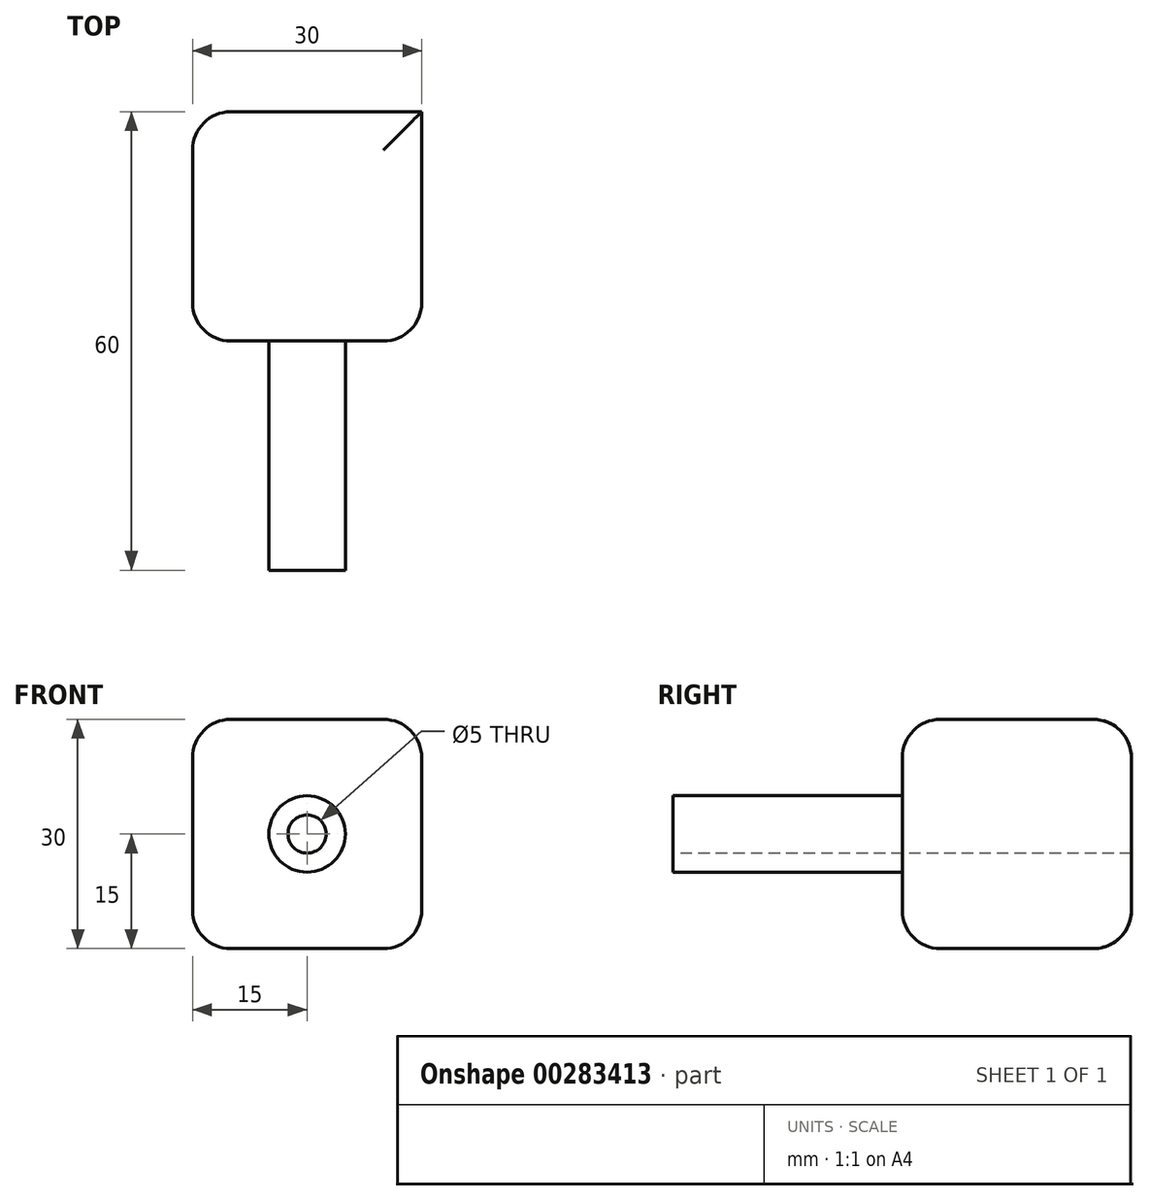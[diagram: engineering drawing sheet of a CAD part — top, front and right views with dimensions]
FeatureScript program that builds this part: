
annotation { "Feature Type Name" : "Feature", "Feature Type Description" : "" }
export const myFeature = defineFeature(function(context is Context, id is Id, definition is map)
    precondition{}
    {
        {
            var Q0;
            Q0=qCreatedBy(makeId("Front.planeOp"),FACE);
            var sketch = newSketch(context, id + "F0", { "sketchPlane" : qUnion([Q0])});
            skLineSegment(sketch, "E0.bottom", {"start": v(15, -15) * mm, "end": v(-15, -15) * mm});
            skLineSegment(sketch, "E0.top", {"start": v(15, 15) * mm, "end": v(-15, 15) * mm});
            skLineSegment(sketch, "E0.left", {"start": v(15, -15) * mm, "end": v(15, 15) * mm});
            skLineSegment(sketch, "E0.right", {"start": v(-15, -15) * mm, "end": v(-15, 15) * mm});
            skPoint(sketch, "E0.middle", {"position": v(0, 0) * mm});
            skSolve(sketch);
        }
        {
            var Q0;
            Q0 = qSketchRegion(id + "F0", true);
            extrude(context, id + "F1", {"entities" : qUnion([Q0]), "oppositeDirection" : true, "depth" : 30 * mm});
        }
        {
            var Q0;
            Q0=makeQuery(id+"F1.opExtrude","CAP_FACE",FACE,{"disambiguationData":[OSD([sQuery(id+"F0.wireOp",EDGE,"E0.bottom"),sQuery(id+"F0.wireOp",EDGE,"E0.top"),sQuery(id+"F0.wireOp",EDGE,"E0.left"),sQuery(id+"F0.wireOp",EDGE,"E0.right")])],"isStart":true});
            var sketch = newSketch(context, id + "F2", { "sketchPlane" : qUnion([Q0])});
            skCircle(sketch, "E1", {"center": v(0, 0) * mm, "radius": 5 * mm});
            skSolve(sketch);
        }
        {
            var Q0;
            Q0 = qSketchRegion(id + "F2", true);
            extrude(context, id + "F3", {"entities" : qUnion([Q0]), "operationType" : NewBodyOperationType.ADD, "depth" : 30 * mm});
        }
        {
            var Q0;
            Q0=makeQuery(id+"F3.opExtrude","CAP_FACE",FACE,{"disambiguationData":[OSD([sQuery(id+"F2.wireOp",EDGE,"E1")])],"isStart":false});
            var sketch = newSketch(context, id + "F4", { "sketchPlane" : qUnion([Q0])});
            skCircle(sketch, "E2", {"center": v(0, 0) * mm, "radius": 2.5 * mm});
            skSolve(sketch);
        }
        {
            var Q0;
            Q0=makeQuery(id+"F4.imprint","IMPRINT",FACE,{"disambiguationData":[TD([[makeQuery(id+"F4.imprint","IMPRINT",EDGE,{"derivedFrom":sQuery(id+"F4.wireOp",EDGE,"E2")}),1.0]])]});
            extrude(context, id + "F5", {"entities" : qUnion([Q0]), "operationType" : NewBodyOperationType.REMOVE, "endBound" : BoundingType.THROUGH_ALL, "oppositeDirection" : true, "depth" : 25 * mm});
        }
        {
            var Q0;
            Q0=makeQuery(id+"F1.opExtrude","CAP_EDGE",EDGE,{"disambiguationData":[OSD([sQuery(id+"F0.wireOp",EDGE,"E0.right")])],"isStart":true});
            var Q1;
            Q1=makeQuery(id+"F1.opExtrude","CAP_EDGE",EDGE,{"disambiguationData":[OSD([sQuery(id+"F0.wireOp",EDGE,"E0.bottom")])],"isStart":true});
            var Q2;
            Q2=makeQuery(id+"F1.opExtrude","CAP_EDGE",EDGE,{"disambiguationData":[OSD([sQuery(id+"F0.wireOp",EDGE,"E0.top")])],"isStart":true});
            var Q3;
            Q3=makeQuery(id+"F1.opExtrude","CAP_EDGE",EDGE,{"disambiguationData":[OSD([sQuery(id+"F0.wireOp",EDGE,"E0.left")])],"isStart":true});
            var Q4;
            Q4=makeQuery(id+"F1.opExtrude","SWEPT_EDGE",EDGE,{"disambiguationData":[OSD([sQuery(id+"F0.wireOp",EDGE,"E0.top"),sQuery(id+"F0.wireOp",EDGE,"E0.right")])]});
            var Q5;
            Q5=makeQuery(id+"F1.opExtrude","SWEPT_EDGE",EDGE,{"disambiguationData":[OSD([sQuery(id+"F0.wireOp",EDGE,"E0.top"),sQuery(id+"F0.wireOp",EDGE,"E0.left")])]});
            var Q6;
            Q6=makeQuery(id+"F1.opExtrude","CAP_EDGE",EDGE,{"disambiguationData":[OSD([sQuery(id+"F0.wireOp",EDGE,"E0.top")])],"isStart":false});
            var Q7;
            Q7=makeQuery(id+"F1.opExtrude","CAP_EDGE",EDGE,{"disambiguationData":[OSD([sQuery(id+"F0.wireOp",EDGE,"E0.right")])],"isStart":false});
            var Q8;
            Q8=makeQuery(id+"F1.opExtrude","SWEPT_EDGE",EDGE,{"disambiguationData":[OSD([sQuery(id+"F0.wireOp",EDGE,"E0.bottom"),sQuery(id+"F0.wireOp",EDGE,"E0.right")])]});
            var Q9;
            Q9=makeQuery(id+"F1.opExtrude","CAP_EDGE",EDGE,{"disambiguationData":[OSD([sQuery(id+"F0.wireOp",EDGE,"E0.bottom")])],"isStart":false});
            var Q10;
            Q10=makeQuery(id+"F1.opExtrude","SWEPT_EDGE",EDGE,{"disambiguationData":[OSD([sQuery(id+"F0.wireOp",EDGE,"E0.bottom"),sQuery(id+"F0.wireOp",EDGE,"E0.left")])]});
            fillet(context, id + "F6", {"entities" : qUnion([Q0, Q1, Q2, Q3, Q4, Q5, Q6, Q7, Q8, Q9, Q10]), "radius" : 5 * mm, "tangentPropagation" : true, "allowEdgeOverflow" : false});
        }
    });
